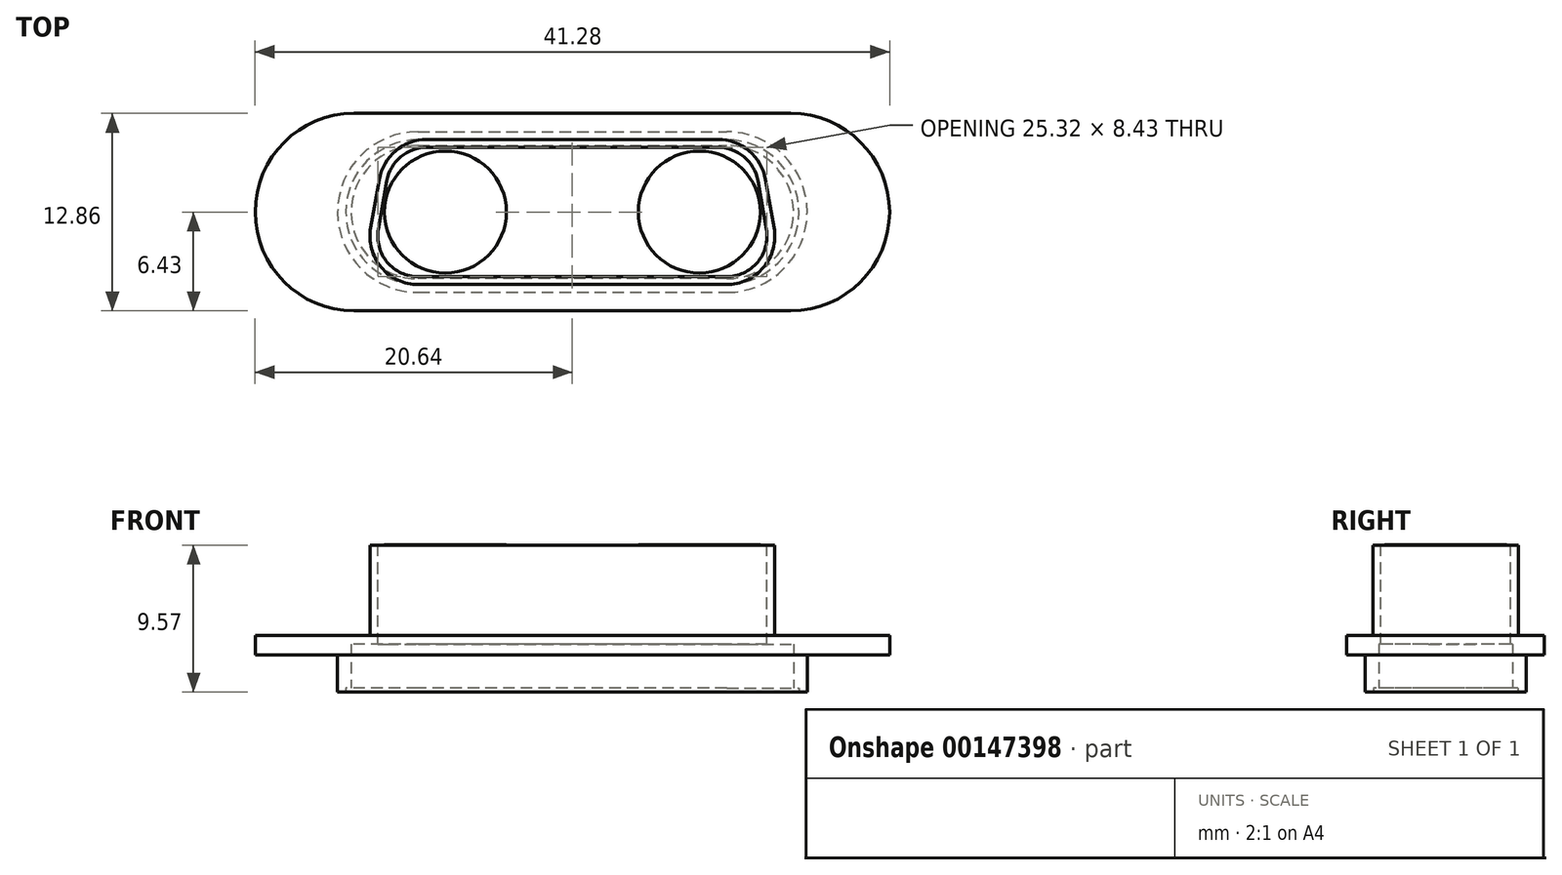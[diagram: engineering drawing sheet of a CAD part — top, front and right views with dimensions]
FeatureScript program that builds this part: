
annotation { "Feature Type Name" : "Feature", "Feature Type Description" : "" }
export const myFeature = defineFeature(function(context is Context, id is Id, definition is map)
    precondition{}
    {
        {
            var Q0;
            Q0=qCreatedBy(makeId("Top.planeOp"),FACE);
            var sketch = newSketch(context, id + "F0", { "sketchPlane" : qUnion([Q0])});
            skLineSegment(sketch, "E0", {"start": v(-14.21, 0) * mm, "end": v(14.21, 0) * mm, "construction": true});
            skArc(sketch, "E1.0.startCap", {"start": v(-14.21, -6.43) * mm, "mid": v(-20.64, 0) * mm, "end": v(-14.21, 6.43) * mm});
            skArc(sketch, "E1.0.endCap", {"start": v(14.21, 6.43) * mm, "mid": v(20.64, 0) * mm, "end": v(14.21, -6.43) * mm});
            skLineSegment(sketch, "E1.0.left", {"start": v(-14.21, 6.43) * mm, "end": v(14.21, 6.43) * mm});
            skLineSegment(sketch, "E1.0.right", {"start": v(-14.21, -6.43) * mm, "end": v(14.21, -6.43) * mm});
            skSolve(sketch);
        }
        {
            var Q0;
            Q0 = qSketchRegion(id + "F0", true);
            extrude(context, id + "F1", {"entities" : qUnion([Q0]), "depth" : 1.27 * mm});
        }
        {
            var Q0;
            Q0=makeQuery(id+"F1.opExtrude","CAP_FACE",FACE,{"disambiguationData":[OSD([sQuery(id+"F0.wireOp",EDGE,"E1.0.startCap"),sQuery(id+"F0.wireOp",EDGE,"E1.0.endCap"),sQuery(id+"F0.wireOp",EDGE,"E1.0.left"),sQuery(id+"F0.wireOp",EDGE,"E1.0.right")])],"isStart":true});
            var sketch = newSketch(context, id + "F2", { "sketchPlane" : qUnion([Q0])});
            skLineSegment(sketch, "E2", {"start": v(-10.05, 0) * mm, "end": v(10.05, 0) * mm, "construction": true});
            skArc(sketch, "E3.0.startCap", {"start": v(-10.05, -5.23) * mm, "mid": v(-15.28, 0) * mm, "end": v(-10.05, 5.23) * mm});
            skArc(sketch, "E3.0.endCap", {"start": v(10.05, 5.23) * mm, "mid": v(15.28, 0) * mm, "end": v(10.05, -5.23) * mm});
            skLineSegment(sketch, "E3.0.left", {"start": v(-10.05, 5.23) * mm, "end": v(10.05, 5.23) * mm});
            skLineSegment(sketch, "E3.0.right", {"start": v(-10.05, -5.23) * mm, "end": v(10.05, -5.23) * mm});
            skSolve(sketch);
        }
        {
            var Q0;
            Q0 = qSketchRegion(id + "F2", true);
            extrude(context, id + "F3", {"entities" : qUnion([Q0]), "operationType" : NewBodyOperationType.ADD, "depth" : 2.41 * mm});
        }
        {
            var Q0;
            Q0=makeQuery(id+"F3.opExtrude","CAP_FACE",FACE,{"disambiguationData":[OSD([sQuery(id+"F2.wireOp",EDGE,"E3.0.startCap"),sQuery(id+"F2.wireOp",EDGE,"E3.0.endCap"),sQuery(id+"F2.wireOp",EDGE,"E3.0.left"),sQuery(id+"F2.wireOp",EDGE,"E3.0.right")])],"isStart":false});
            var sketch = newSketch(context, id + "F4", { "sketchPlane" : qUnion([Q0])});
            skArc(sketch, "E4.0.0", {"start": v(-10.05, 5.23) * mm, "mid": v(-15.28, 0) * mm, "end": v(-10.05, -5.23) * mm});
            skLineSegment(sketch, "E4.0.1", {"start": v(-10.05, -5.23) * mm, "end": v(10.05, -5.23) * mm});
            skArc(sketch, "E4.0.2", {"start": v(10.05, -5.23) * mm, "mid": v(15.28, 0) * mm, "end": v(10.05, 5.23) * mm});
            skLineSegment(sketch, "E4.0.3", {"start": v(10.05, 5.23) * mm, "end": v(-10.05, 5.23) * mm});
            skLineSegment(sketch, "E5.0", {"start": v(10.05, 4.34) * mm, "end": v(-10.05, 4.34) * mm});
            skArc(sketch, "E5.1", {"start": v(10.05, -4.34) * mm, "mid": v(14.39, 0) * mm, "end": v(10.05, 4.34) * mm});
            skLineSegment(sketch, "E5.2", {"start": v(-10.05, -4.34) * mm, "end": v(10.05, -4.34) * mm});
            skArc(sketch, "E5.3", {"start": v(-10.05, 4.34) * mm, "mid": v(-14.39, 0) * mm, "end": v(-10.05, -4.34) * mm});
            skLineSegment(sketch, "E6.0", {"start": v(10.05, 4.7) * mm, "end": v(-10.05, 4.7) * mm});
            skArc(sketch, "E6.1", {"start": v(10.05, -4.7) * mm, "mid": v(14.74, 0) * mm, "end": v(10.05, 4.7) * mm});
            skLineSegment(sketch, "E6.2", {"start": v(-10.05, -4.7) * mm, "end": v(10.05, -4.7) * mm});
            skArc(sketch, "E6.3", {"start": v(-10.05, 4.7) * mm, "mid": v(-14.74, 0) * mm, "end": v(-10.05, -4.7) * mm});
            skSolve(sketch);
        }
        {
            var Q0;
            Q0=makeQuery(id+"F4.imprint","IMPRINT",FACE,{"disambiguationData":[TD([[makeQuery(id+"F4.imprint","IMPRINT",EDGE,{"derivedFrom":sQuery(id+"F4.wireOp",EDGE,"E5.0")}),1.0]])]});
            extrude(context, id + "F5", {"entities" : qUnion([Q0]), "operationType" : NewBodyOperationType.REMOVE, "oppositeDirection" : true, "depth" : 3.1 * mm});
        }
        {
            var Q0;
            Q0=makeQuery(id+"F4.imprint","IMPRINT",FACE,{"disambiguationData":[TD([[makeQuery(id+"F4.imprint","IMPRINT",EDGE,{"derivedFrom":sQuery(id+"F4.wireOp",EDGE,"E5.0")}),-1.0]])]});
            extrude(context, id + "F6", {"entities" : qUnion([Q0]), "operationType" : NewBodyOperationType.REMOVE, "oppositeDirection" : true, "depth" : 0.25 * mm});
        }
        {
            var Q0;
            Q0=makeQuery(id+"F1.opExtrude","CAP_FACE",FACE,{"disambiguationData":[OSD([sQuery(id+"F0.wireOp",EDGE,"E1.0.startCap"),sQuery(id+"F0.wireOp",EDGE,"E1.0.endCap"),sQuery(id+"F0.wireOp",EDGE,"E1.0.left"),sQuery(id+"F0.wireOp",EDGE,"E1.0.right")])],"isStart":false});
            var sketch = newSketch(context, id + "F7", { "sketchPlane" : qUnion([Q0])});
            skLineSegment(sketch, "E7", {"start": v(-6.72, 0) * mm, "end": v(6.72, 0) * mm, "construction": true});
            skLineSegment(sketch, "E8", {"start": v(-9.46, 4.22) * mm, "end": v(9.46, 4.22) * mm});
            skLineSegment(sketch, "E9", {"start": v(10.02, -4.22) * mm, "end": v(-10.02, -4.22) * mm});
            skLineSegment(sketch, "E10", {"start": v(-12.07, 2.03) * mm, "end": v(-12.62, -1.12) * mm});
            skLineSegment(sketch, "E11", {"start": v(12.07, 2.03) * mm, "end": v(12.62, -1.12) * mm});
            skPoint(sketch, "E12.visualSharp", {"position": v(-11.68, 4.22) * mm});
            skArc(sketch, "E12.filletArc", {"start": v(-9.46, 4.22) * mm, "mid": v(-11.16, 3.6) * mm, "end": v(-12.07, 2.03) * mm});
            skPoint(sketch, "E13.visualSharp", {"position": v(11.68, 4.22) * mm});
            skArc(sketch, "E13.filletArc", {"start": v(12.07, 2.03) * mm, "mid": v(11.16, 3.6) * mm, "end": v(9.46, 4.22) * mm});
            skPoint(sketch, "E14.visualSharp", {"position": v(13.17, -4.22) * mm});
            skArc(sketch, "E14.filletArc", {"start": v(10.02, -4.22) * mm, "mid": v(12.04, -3.27) * mm, "end": v(12.62, -1.12) * mm});
            skPoint(sketch, "E15.visualSharp", {"position": v(-13.17, -4.22) * mm});
            skArc(sketch, "E15.filletArc", {"start": v(-12.62, -1.12) * mm, "mid": v(-12.04, -3.27) * mm, "end": v(-10.02, -4.22) * mm});
            skArc(sketch, "E16.0", {"start": v(-9.46, 4.72) * mm, "mid": v(-11.49, 3.99) * mm, "end": v(-12.57, 2.12) * mm});
            skLineSegment(sketch, "E16.1", {"start": v(-12.57, 2.12) * mm, "end": v(-13.12, -1.03) * mm});
            skLineSegment(sketch, "E16.2", {"start": v(-9.46, 4.72) * mm, "end": v(9.46, 4.72) * mm});
            skArc(sketch, "E16.3", {"start": v(-13.12, -1.03) * mm, "mid": v(-12.43, -3.6) * mm, "end": v(-10.02, -4.72) * mm});
            skArc(sketch, "E16.4", {"start": v(12.57, 2.12) * mm, "mid": v(11.49, 3.99) * mm, "end": v(9.46, 4.72) * mm});
            skLineSegment(sketch, "E16.5", {"start": v(12.57, 2.12) * mm, "end": v(13.12, -1.03) * mm});
            skArc(sketch, "E16.6", {"start": v(10.02, -4.72) * mm, "mid": v(12.43, -3.6) * mm, "end": v(13.12, -1.03) * mm});
            skLineSegment(sketch, "E16.7", {"start": v(10.02, -4.72) * mm, "end": v(-10.02, -4.72) * mm});
            skSolve(sketch);
        }
        {
            var Q0;
            Q0=makeQuery(id+"F7.imprint","IMPRINT",FACE,{"disambiguationData":[TD([[makeQuery(id+"F7.imprint","IMPRINT",EDGE,{"derivedFrom":sQuery(id+"F7.wireOp",EDGE,"E8")}),-1.0]])]});
            extrude(context, id + "F8", {"entities" : qUnion([Q0]), "operationType" : NewBodyOperationType.REMOVE, "endBound" : BoundingType.THROUGH_ALL, "oppositeDirection" : true, "depth" : 25.4 * mm, "hasSecondDirection" : true, "secondDirectionBound" : BoundingType.THROUGH_ALL, "secondDirectionOppositeDirection" : false, "secondDirectionDepth" : 25.4 * mm});
        }
        {
            var Q0;
            Q0=makeQuery(id+"F7.imprint","IMPRINT",FACE,{"disambiguationData":[TD([[makeQuery(id+"F7.imprint","IMPRINT",EDGE,{"derivedFrom":sQuery(id+"F7.wireOp",EDGE,"E8")}),1.0]])]});
            extrude(context, id + "F9", {"entities" : qUnion([Q0]), "operationType" : NewBodyOperationType.ADD, "depth" : 5.87 * mm});
        }
        {
            var Q0;
            Q0=makeQuery(id+"F9.opExtrude","CAP_FACE",FACE,{"disambiguationData":[OSD([sQuery(id+"F7.wireOp",EDGE,"E8"),sQuery(id+"F7.wireOp",EDGE,"E9"),sQuery(id+"F7.wireOp",EDGE,"E10"),sQuery(id+"F7.wireOp",EDGE,"E11"),sQuery(id+"F7.wireOp",EDGE,"E12.filletArc"),sQuery(id+"F7.wireOp",EDGE,"E13.filletArc"),sQuery(id+"F7.wireOp",EDGE,"E14.filletArc"),sQuery(id+"F7.wireOp",EDGE,"E15.filletArc"),sQuery(id+"F7.wireOp",EDGE,"E16.0"),sQuery(id+"F7.wireOp",EDGE,"E16.1"),sQuery(id+"F7.wireOp",EDGE,"E16.2"),sQuery(id+"F7.wireOp",EDGE,"E16.3"),sQuery(id+"F7.wireOp",EDGE,"E16.4"),sQuery(id+"F7.wireOp",EDGE,"E16.5"),sQuery(id+"F7.wireOp",EDGE,"E16.6"),sQuery(id+"F7.wireOp",EDGE,"E16.7")])],"isStart":false});
            var sketch = newSketch(context, id + "F10", { "sketchPlane" : qUnion([Q0])});
            skLineSegment(sketch, "E17.0", {"start": v(-9.46, 4.22) * mm, "end": v(9.46, 4.22) * mm});
            skArc(sketch, "E17.1", {"start": v(-9.46, 4.22) * mm, "mid": v(-11.16, 3.6) * mm, "end": v(-12.07, 2.03) * mm});
            skLineSegment(sketch, "E17.2", {"start": v(-12.07, 2.03) * mm, "end": v(-12.62, -1.12) * mm});
            skArc(sketch, "E17.3", {"start": v(-12.62, -1.12) * mm, "mid": v(-12.04, -3.27) * mm, "end": v(-10.02, -4.22) * mm});
            skLineSegment(sketch, "E17.4", {"start": v(10.02, -4.22) * mm, "end": v(-10.02, -4.22) * mm});
            skArc(sketch, "E17.5", {"start": v(10.02, -4.22) * mm, "mid": v(12.04, -3.27) * mm, "end": v(12.62, -1.12) * mm});
            skLineSegment(sketch, "E17.6", {"start": v(12.07, 2.03) * mm, "end": v(12.62, -1.12) * mm});
            skArc(sketch, "E17.7", {"start": v(12.07, 2.03) * mm, "mid": v(11.16, 3.6) * mm, "end": v(9.46, 4.22) * mm});
            skArc(sketch, "E18.0", {"start": v(-9.46, 4.09) * mm, "mid": v(-11.08, 3.5) * mm, "end": v(-11.94, 2.01) * mm});
            skLineSegment(sketch, "E18.1", {"start": v(-11.94, 2.01) * mm, "end": v(-12.5, -1.14) * mm});
            skLineSegment(sketch, "E18.2", {"start": v(-9.46, 4.09) * mm, "end": v(9.46, 4.09) * mm});
            skArc(sketch, "E18.3", {"start": v(-12.5, -1.14) * mm, "mid": v(-11.95, -3.2) * mm, "end": v(-10.02, -4.09) * mm});
            skArc(sketch, "E18.4", {"start": v(11.94, 2.01) * mm, "mid": v(11.08, 3.5) * mm, "end": v(9.46, 4.09) * mm});
            skLineSegment(sketch, "E18.5", {"start": v(11.94, 2.01) * mm, "end": v(12.5, -1.14) * mm});
            skArc(sketch, "E18.6", {"start": v(10.02, -4.09) * mm, "mid": v(11.95, -3.2) * mm, "end": v(12.5, -1.14) * mm});
            skLineSegment(sketch, "E18.7", {"start": v(10.02, -4.09) * mm, "end": v(-10.02, -4.09) * mm});
            skCircle(sketch, "E19", {"center": v(-8.27, 0) * mm, "radius": 3.97 * mm});
            skCircle(sketch, "E20", {"center": v(8.27, 0) * mm, "radius": 3.97 * mm});
            skLineSegment(sketch, "E21", {"start": v(-8.27, 0) * mm, "end": v(8.27, 0) * mm, "construction": true});
            skSolve(sketch);
        }
        {
            var Q0;
            Q0=makeQuery(id+"F10.imprint","IMPRINT",FACE,{"disambiguationData":[TD([[makeQuery(id+"F10.imprint","IMPRINT",EDGE,{"derivedFrom":sQuery(id+"F10.wireOp",EDGE,"E19")}),1.0]])]});
            var Q1;
            Q1=makeQuery(id+"F10.imprint","IMPRINT",FACE,{"disambiguationData":[TD([[makeQuery(id+"F10.imprint","IMPRINT",EDGE,{"derivedFrom":sQuery(id+"F10.wireOp",EDGE,"E20")}),1.0]])]});
            extrude(context, id + "F11", {"entities" : qUnion([Q0, Q1]), "depth" : 0.03 * mm});
        }
    });
